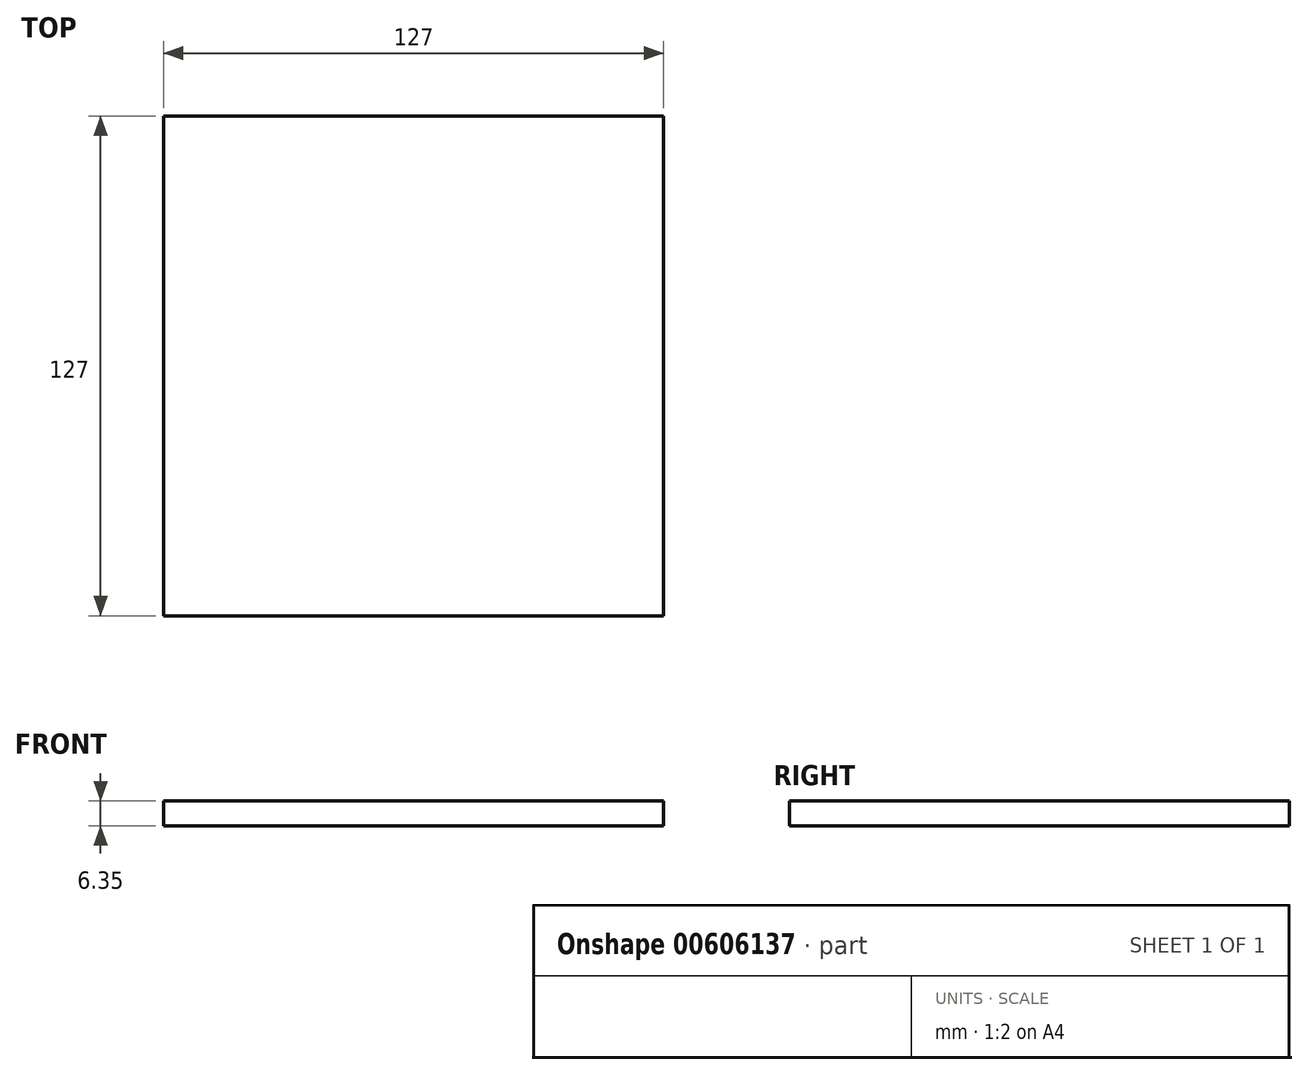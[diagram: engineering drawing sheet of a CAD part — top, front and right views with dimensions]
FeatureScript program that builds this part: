
annotation { "Feature Type Name" : "Feature", "Feature Type Description" : "" }
export const myFeature = defineFeature(function(context is Context, id is Id, definition is map)
    precondition{}
    {
        {
            var Q0;
            Q0=qCreatedBy(makeId("Front.planeOp"),FACE);
            var sketch = newSketch(context, id + "F0", { "sketchPlane" : qUnion([Q0])});
            skLineSegment(sketch, "E0.bottom", {"start": v(-61, 0) * mm, "end": v(66, 0) * mm});
            skLineSegment(sketch, "E0.top", {"start": v(-61, -6.35) * mm, "end": v(66, -6.35) * mm});
            skLineSegment(sketch, "E0.left", {"start": v(-61, 0) * mm, "end": v(-61, -6.35) * mm});
            skLineSegment(sketch, "E0.right", {"start": v(66, 0) * mm, "end": v(66, -6.35) * mm});
            skSolve(sketch);
        }
        {
            var Q0;
            Q0=makeQuery(id+"F0.imprint","IMPRINT",FACE,{"disambiguationData":[TD([[makeQuery(id+"F0.imprint","IMPRINT",EDGE,{"derivedFrom":sQuery(id+"F0.wireOp",EDGE,"E0.bottom")}),-1.0]])]});
            extrude(context, id + "F1", {"entities" : qUnion([Q0]), "depth" : 127 * mm, "offsetDistance" : 25.4 * mm});
        }
    });
